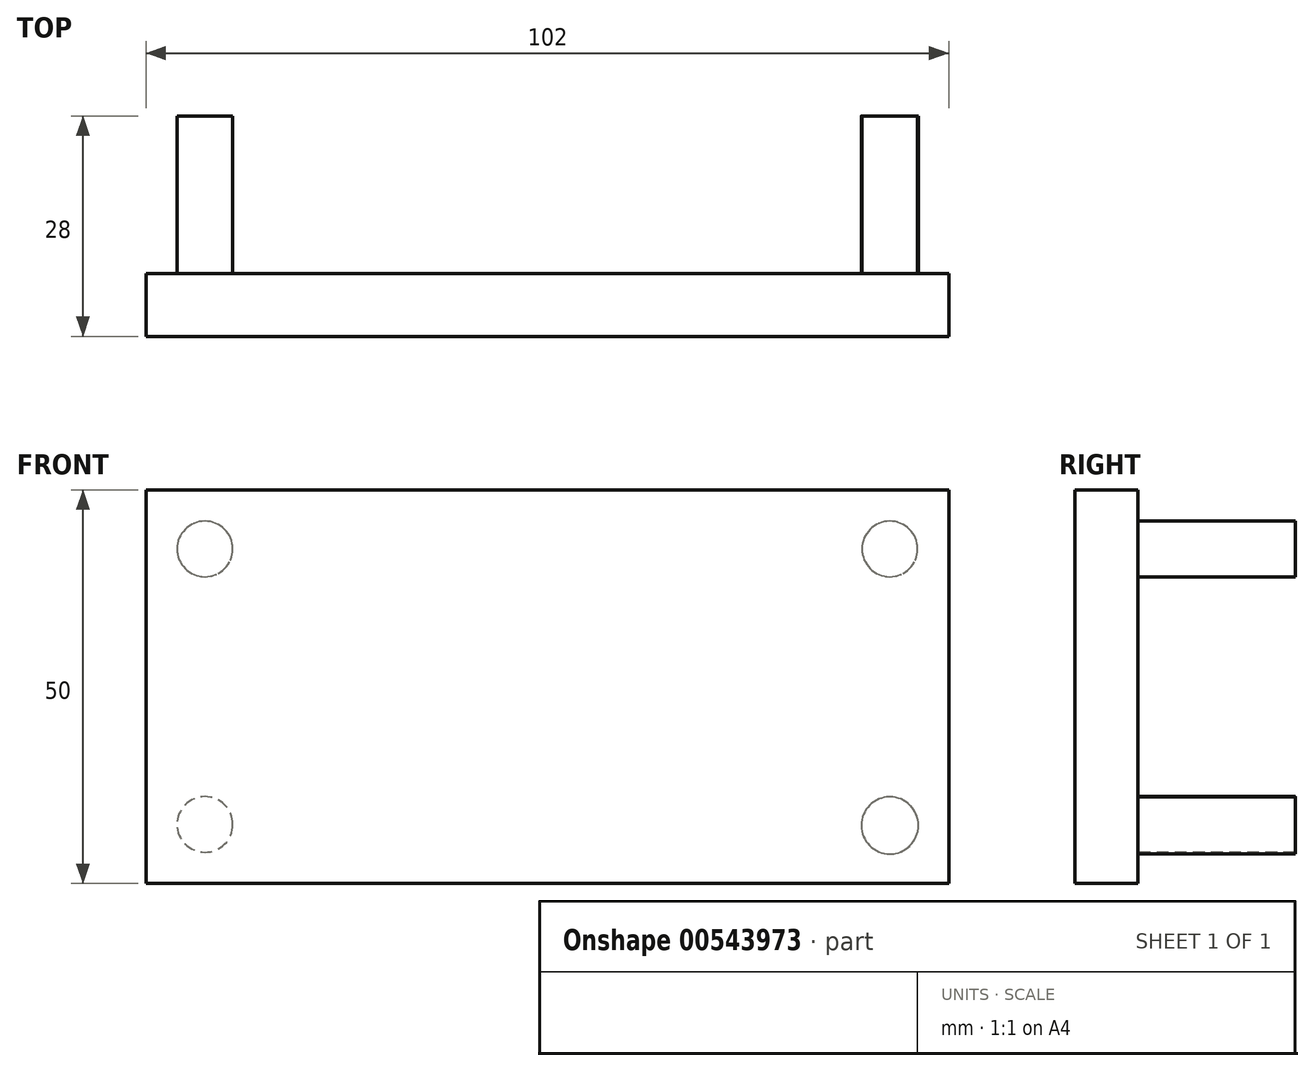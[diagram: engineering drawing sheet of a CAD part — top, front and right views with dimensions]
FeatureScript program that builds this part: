
annotation { "Feature Type Name" : "Feature", "Feature Type Description" : "" }
export const myFeature = defineFeature(function(context is Context, id is Id, definition is map)
    precondition{}
    {
        {
            var Q0;
            Q0=qCreatedBy(makeId("Front.planeOp"),FACE);
            var sketch = newSketch(context, id + "F0", { "sketchPlane" : qUnion([Q0])});
            skLineSegment(sketch, "E0.bottom", {"start": v(-51, 25) * mm, "end": v(51, 25) * mm});
            skLineSegment(sketch, "E0.top", {"start": v(-51, -25) * mm, "end": v(51, -25) * mm});
            skLineSegment(sketch, "E0.left", {"start": v(-51, 25) * mm, "end": v(-51, -25) * mm});
            skLineSegment(sketch, "E0.right", {"start": v(51, 25) * mm, "end": v(51, -25) * mm});
            skPoint(sketch, "E0.middle", {"position": v(0, 0) * mm});
            skSolve(sketch);
        }
        {
            var Q0;
            Q0=makeQuery(id+"F0.imprint","IMPRINT",FACE,{"disambiguationData":[TD([[makeQuery(id+"F0.imprint","IMPRINT",EDGE,{"derivedFrom":sQuery(id+"F0.wireOp",EDGE,"E0.bottom")}),-1.0]])]});
            extrude(context, id + "F1", {"entities" : qUnion([Q0]), "endBound" : BoundingType.SYMMETRIC, "depth" : 8 * mm, "offsetDistance" : 25 * mm});
        }
        {
            var Q0;
            Q0=makeQuery(id+"F1.opExtrude","CAP_FACE",FACE,{"disambiguationData":[OSD([sQuery(id+"F0.wireOp",EDGE,"E0.bottom"),sQuery(id+"F0.wireOp",EDGE,"E0.top"),sQuery(id+"F0.wireOp",EDGE,"E0.left"),sQuery(id+"F0.wireOp",EDGE,"E0.right")])],"isStart":true});
            var sketch = newSketch(context, id + "F2", { "sketchPlane" : qUnion([Q0])});
            skLineSegment(sketch, "E1.left", {"start": v(51, -25) * mm, "end": v(51, -15) * mm});
            skLineSegment(sketch, "E2.right", {"start": v(-41, -20.25) * mm, "end": v(-41, -20) * mm});
            skCircle(sketch, "E3", {"center": v(43.5, -17.5) * mm, "radius": 3.54 * mm});
            skPoint(sketch, "E3.first.point", {"position": v(41, -20) * mm});
            skPoint(sketch, "E3.second.point", {"position": v(46, -15) * mm});
            skPoint(sketch, "E3.third.point", {"position": v(46, -20) * mm});
            skPoint(sketch, "E3.third.point.positionSnap0", {"position": v(46, -15) * mm});
            skPoint(sketch, "E3.third.point.positionSnap1", {"position": v(41, -20) * mm});
            skCircle(sketch, "E4", {"center": v(43.5, 17.5) * mm, "radius": 3.54 * mm});
            skPoint(sketch, "E4.second.point", {"position": v(46, 20) * mm});
            skPoint(sketch, "E4.second.point.positionSnap0", {"position": v(41, 20) * mm});
            skPoint(sketch, "E4.third.point", {"position": v(46, 15) * mm});
            skCircle(sketch, "E5", {"center": v(-43.5, 17.5) * mm, "radius": 3.54 * mm});
            skPoint(sketch, "E5.second.point", {"position": v(-46, 20) * mm});
            skPoint(sketch, "E5.second.point.positionSnap0", {"position": v(-46, 15) * mm});
            skPoint(sketch, "E5.second.point.positionSnap1", {"position": v(-41, 20) * mm});
            skPoint(sketch, "E5.third.point", {"position": v(-41, 20) * mm});
            skCircle(sketch, "E6", {"center": v(-43.5, -17.63) * mm, "radius": 3.63 * mm});
            skPoint(sketch, "E6.second.point", {"position": v(-46.24, -20) * mm});
            skPoint(sketch, "E6.second.point.positionSnap0", {"position": v(-41, -20) * mm});
            skPoint(sketch, "E6.third.point", {"position": v(-46, -15) * mm});
            skPoint(sketch, "E7.orphan", {"position": v(41, 15) * mm});
            skPoint(sketch, "E8.left.end.orphan", {"position": v(51, 15) * mm});
            skPoint(sketch, "E8.bottom.end.orphan", {"position": v(41, 25) * mm});
            skPoint(sketch, "E9.orphan", {"position": v(41, -25) * mm});
            skPoint(sketch, "E1.right.end.orphan", {"position": v(41, -15) * mm});
            skPoint(sketch, "E2.bottom.end.orphan", {"position": v(-41, -25) * mm});
            skPoint(sketch, "E2.left.end.orphan", {"position": v(-51, -15) * mm});
            skPoint(sketch, "E10.orphan", {"position": v(-41, -15) * mm});
            skPoint(sketch, "E11.bottom.end.orphan", {"position": v(-41, 25) * mm});
            skPoint(sketch, "E11.left.end.orphan", {"position": v(-51, 15) * mm});
            skPoint(sketch, "E11.right.end.orphan", {"position": v(-41, 15) * mm});
            skSolve(sketch);
        }
        {
            var Q0;
            Q0=makeQuery(id+"F2.imprint","IMPRINT",FACE,{"disambiguationData":[TD([[makeQuery(id+"F2.imprint","IMPRINT",EDGE,{"derivedFrom":sQuery(id+"F2.wireOp",EDGE,"E6")}),1.0]])]});
            var Q1;
            Q1=makeQuery(id+"F2.imprint","IMPRINT",FACE,{"disambiguationData":[TD([[makeQuery(id+"F2.imprint","IMPRINT",EDGE,{"derivedFrom":sQuery(id+"F2.wireOp",EDGE,"E5")}),1.0]])]});
            var Q2;
            Q2=makeQuery(id+"F2.imprint","IMPRINT",FACE,{"disambiguationData":[TD([[makeQuery(id+"F2.imprint","IMPRINT",EDGE,{"derivedFrom":sQuery(id+"F2.wireOp",EDGE,"E3")}),1.0]])]});
            var Q3;
            Q3=makeQuery(id+"F2.imprint","IMPRINT",FACE,{"disambiguationData":[TD([[makeQuery(id+"F2.imprint","IMPRINT",EDGE,{"derivedFrom":sQuery(id+"F2.wireOp",EDGE,"E4")}),1.0]])]});
            extrude(context, id + "F3", {"entities" : qUnion([Q0, Q1, Q2, Q3]), "operationType" : NewBodyOperationType.ADD, "depth" : 20 * mm, "offsetDistance" : 25 * mm});
        }
    });
